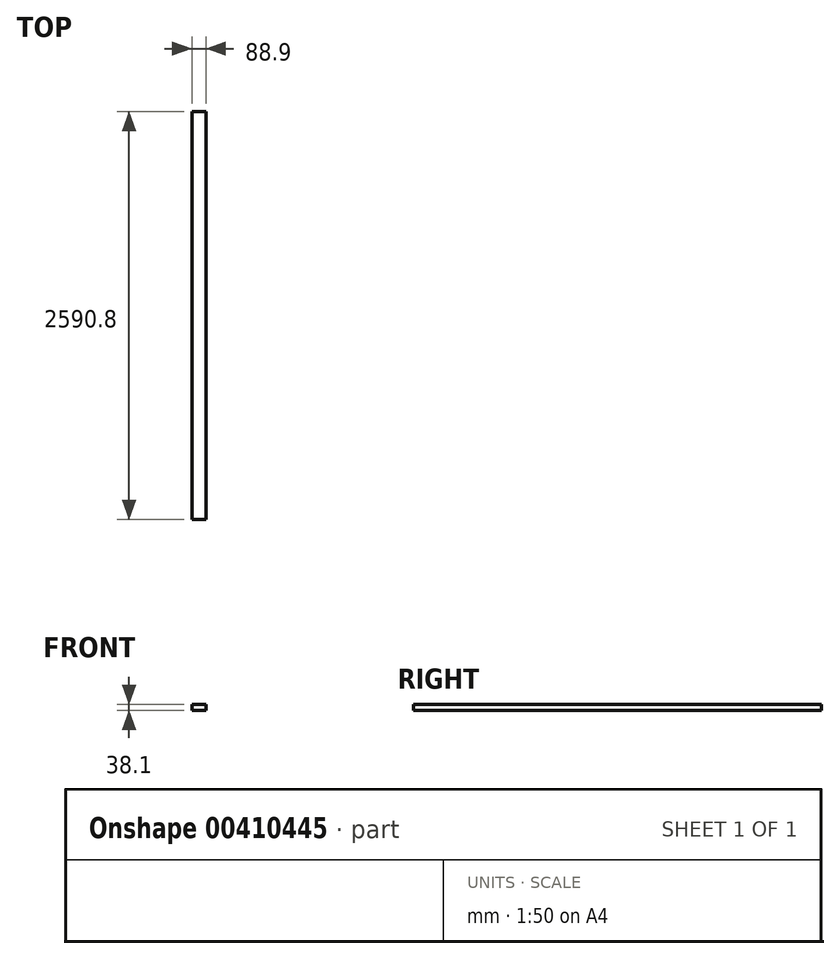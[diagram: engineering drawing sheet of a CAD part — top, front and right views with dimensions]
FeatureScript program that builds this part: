
annotation { "Feature Type Name" : "Feature", "Feature Type Description" : "" }
export const myFeature = defineFeature(function(context is Context, id is Id, definition is map)
    precondition{}
    {
        {
            var Q0;
            Q0=qCreatedBy(makeId("Right.planeOp"),FACE);
            var sketch = newSketch(context, id + "F0", { "sketchPlane" : qUnion([Q0])});
            skLineSegment(sketch, "E0.bottom", {"start": v(-1295.4, 19.05) * mm, "end": v(1295.4, 19.05) * mm});
            skLineSegment(sketch, "E0.top", {"start": v(-1295.4, -19.05) * mm, "end": v(1295.4, -19.05) * mm});
            skLineSegment(sketch, "E0.left", {"start": v(-1295.4, 19.05) * mm, "end": v(-1295.4, -19.05) * mm});
            skLineSegment(sketch, "E0.right", {"start": v(1295.4, 19.05) * mm, "end": v(1295.4, -19.05) * mm});
            skPoint(sketch, "E0.middle", {"position": v(0, 0) * mm});
            skSolve(sketch);
        }
        {
            var Q0;
            Q0 = qSketchRegion(id + "F0", true);
            extrude(context, id + "F1", {"entities" : qUnion([Q0]), "depth" : 88.9 * mm, "offsetDistance" : 25.4 * mm});
        }
    });
